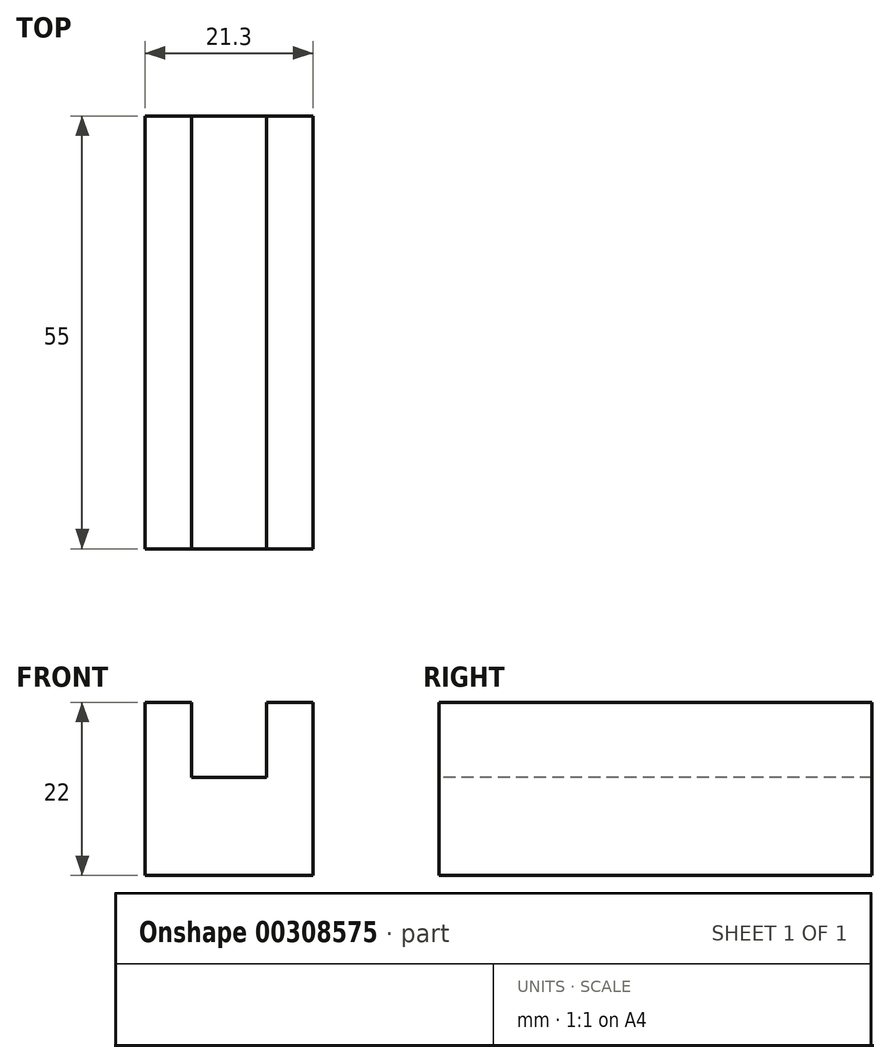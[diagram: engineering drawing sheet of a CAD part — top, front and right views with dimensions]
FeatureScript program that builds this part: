
annotation { "Feature Type Name" : "Feature", "Feature Type Description" : "" }
export const myFeature = defineFeature(function(context is Context, id is Id, definition is map)
    precondition{}
    {
        {
            var Q0;
            Q0=qCreatedBy(makeId("Front.planeOp"),FACE);
            var sketch = newSketch(context, id + "F0", { "sketchPlane" : qUnion([Q0])});
            skLineSegment(sketch, "E0.bottom", {"start": v(0, 0) * mm, "end": v(21.3, 0) * mm});
            skLineSegment(sketch, "E0.top", {"start": v(0, 22) * mm, "end": v(21.3, 22) * mm});
            skLineSegment(sketch, "E0.left", {"start": v(0, 0) * mm, "end": v(0, 22) * mm});
            skLineSegment(sketch, "E0.right", {"start": v(21.3, 0) * mm, "end": v(21.3, 22) * mm});
            skSolve(sketch);
        }
        {
            var Q0;
            Q0=qSketchRegion(id+"F0",true);
            extrude(context, id + "F1", {"entities" : qUnion([Q0]), "oppositeDirection" : true, "depth" : 55 * mm});
        }
        {
            var Q0;
            Q0=makeQuery(id+"F1.opExtrude","CAP_FACE",FACE,{"disambiguationData":[OSD([sQuery(id+"F0.wireOp",EDGE,"E0.bottom"),sQuery(id+"F0.wireOp",EDGE,"E0.top"),sQuery(id+"F0.wireOp",EDGE,"E0.left"),sQuery(id+"F0.wireOp",EDGE,"E0.right")])],"isStart":true});
            var sketch = newSketch(context, id + "F2", { "sketchPlane" : qUnion([Q0])});
            skLineSegment(sketch, "E1", {"start": v(10.65, 22) * mm, "end": v(10.65, 0) * mm, "construction": true});
            skLineSegment(sketch, "E2.bottom", {"start": v(15.41, 22) * mm, "end": v(5.89, 22) * mm});
            skLineSegment(sketch, "E2.top", {"start": v(15.41, 12.48) * mm, "end": v(5.89, 12.48) * mm});
            skLineSegment(sketch, "E2.left", {"start": v(15.41, 22) * mm, "end": v(15.41, 12.48) * mm});
            skLineSegment(sketch, "E2.right", {"start": v(5.89, 22) * mm, "end": v(5.89, 12.48) * mm});
            skPoint(sketch, "E2.middle", {"position": v(10.65, 17.24) * mm});
            skSolve(sketch);
        }
        {
            var Q0;
            Q0=qSketchRegion(id+"F2",true);
            extrude(context, id + "F3", {"entities" : qUnion([Q0]), "operationType" : NewBodyOperationType.REMOVE, "endBound" : BoundingType.THROUGH_ALL, "oppositeDirection" : true, "depth" : 25 * mm});
        }
    });
